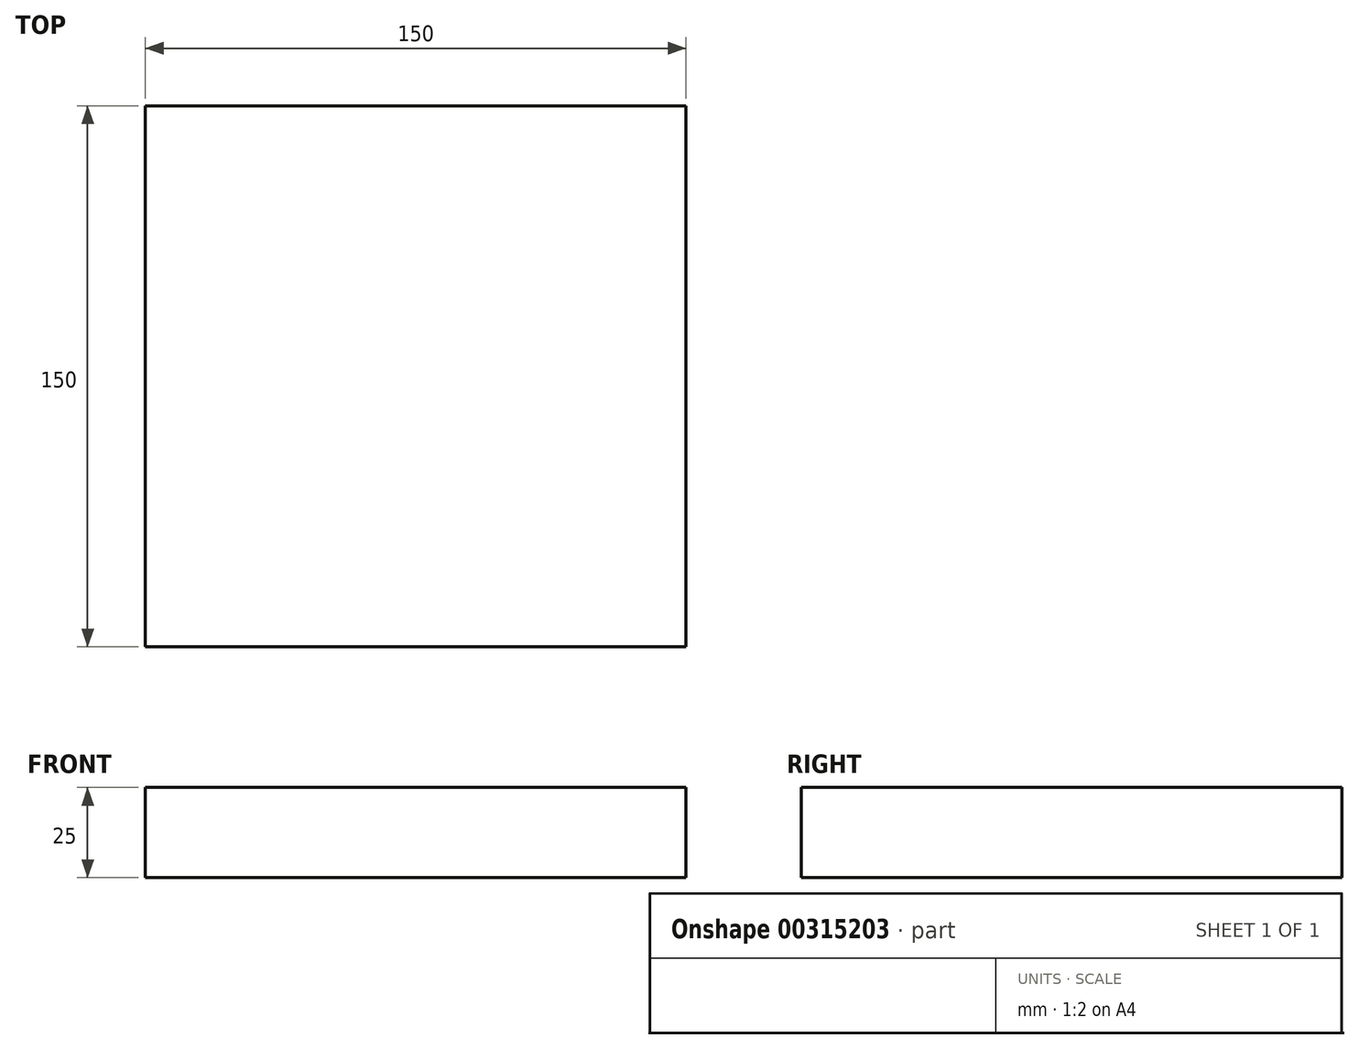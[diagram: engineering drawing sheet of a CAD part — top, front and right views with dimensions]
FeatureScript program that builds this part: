
annotation { "Feature Type Name" : "Feature", "Feature Type Description" : "" }
export const myFeature = defineFeature(function(context is Context, id is Id, definition is map)
    precondition{}
    {
        {
            var Q0;
            Q0=qCreatedBy(makeId("Top.planeOp"),FACE);
            var sketch = newSketch(context, id + "F0", { "sketchPlane" : qUnion([Q0])});
            skLineSegment(sketch, "E0.bottom", {"start": v(75, -75) * mm, "end": v(-75, -75) * mm});
            skLineSegment(sketch, "E0.top", {"start": v(75, 75) * mm, "end": v(-75, 75) * mm});
            skLineSegment(sketch, "E0.left", {"start": v(75, -75) * mm, "end": v(75, 75) * mm});
            skLineSegment(sketch, "E0.right", {"start": v(-75, -75) * mm, "end": v(-75, 75) * mm});
            skPoint(sketch, "E0.middle", {"position": v(0, 0) * mm});
            skSolve(sketch);
        }
        {
            var Q0;
            Q0 = qSketchRegion(id + "F0", true);
            var Q1;
            Q1=makeQuery(id+"F0.imprint","IMPRINT",FACE,{"disambiguationData":[TD([[makeQuery(id+"F0.imprint","IMPRINT",EDGE,{"derivedFrom":sQuery(id+"F0.wireOp",EDGE,"E0.bottom")}),-1.0]])]});
            extrude(context, id + "F1", {"entities" : qUnion([Q0, Q1]), "depth" : 25 * mm});
        }
    });
